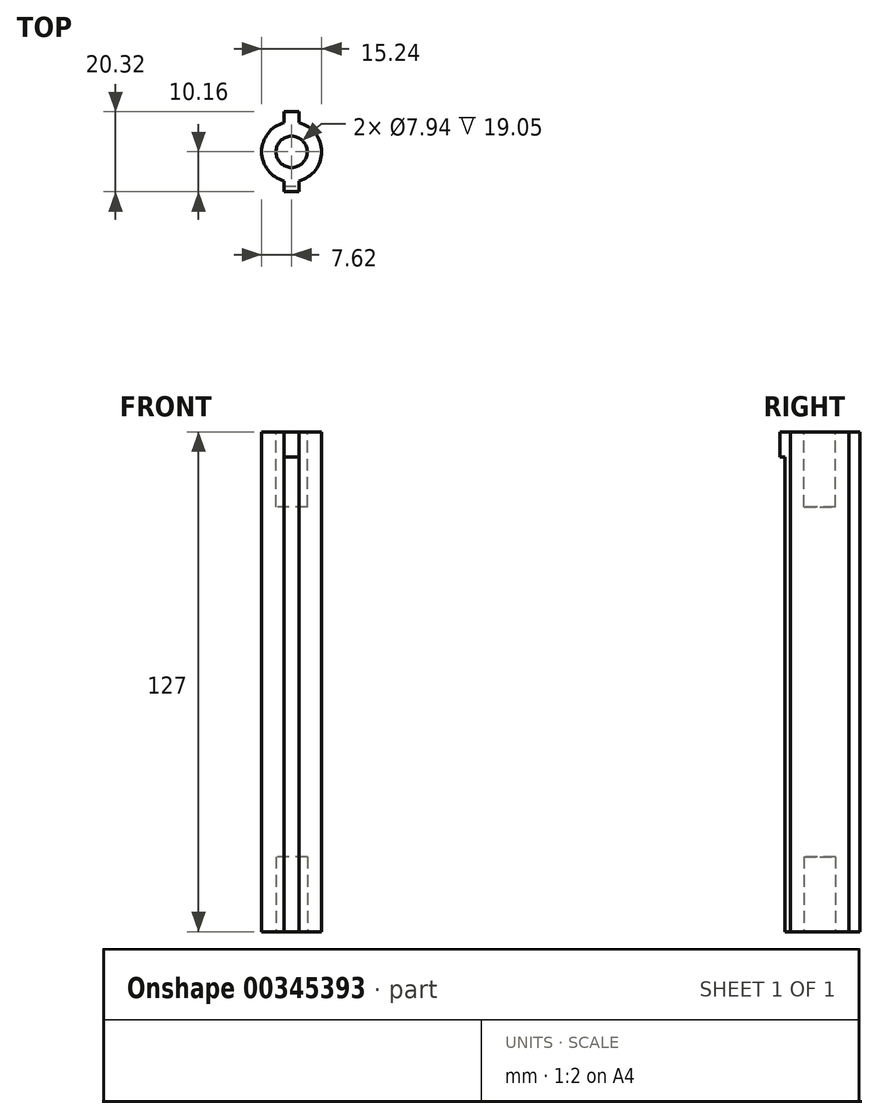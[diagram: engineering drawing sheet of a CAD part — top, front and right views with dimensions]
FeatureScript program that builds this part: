
annotation { "Feature Type Name" : "Feature", "Feature Type Description" : "" }
export const myFeature = defineFeature(function(context is Context, id is Id, definition is map)
    precondition{}
    {
        {
            var Q0;
            Q0=qCreatedBy(makeId("Top.planeOp"),FACE);
            var sketch = newSketch(context, id + "F0", { "sketchPlane" : qUnion([Q0])});
            skCircle(sketch, "E0", {"center": v(0, 0) * mm, "radius": 7.62 * mm});
            skSolve(sketch);
        }
        {
            var Q0;
            Q0=makeQuery(id+"F0.imprint","IMPRINT",FACE,{"disambiguationData":[TD([[makeQuery(id+"F0.imprint","IMPRINT",EDGE,{"derivedFrom":sQuery(id+"F0.wireOp",EDGE,"E0")}),1.0]])]});
            extrude(context, id + "F1", {"entities" : qUnion([Q0]), "depth" : 127 * mm});
        }
        {
            var Q0;
            Q0=makeQuery(id+"F1.opExtrude","CAP_FACE",FACE,{"disambiguationData":[OSD([sQuery(id+"F0.wireOp",EDGE,"E0")])],"isStart":false});
            var sketch = newSketch(context, id + "F2", { "sketchPlane" : qUnion([Q0])});
            skCircle(sketch, "E1", {"center": v(0, 0) * mm, "radius": 3.97 * mm});
            skSolve(sketch);
        }
        {
            var Q0;
            Q0=makeQuery(id+"F2.imprint","IMPRINT",FACE,{"disambiguationData":[TD([[makeQuery(id+"F2.imprint","IMPRINT",EDGE,{"derivedFrom":sQuery(id+"F2.wireOp",EDGE,"E1")}),1.0]])]});
            extrude(context, id + "F3", {"entities" : qUnion([Q0]), "operationType" : NewBodyOperationType.REMOVE, "oppositeDirection" : true, "depth" : 19.05 * mm});
        }
        {
            var Q0;
            Q0=qCreatedBy(makeId("Top.planeOp"),FACE);
            var sketch = newSketch(context, id + "F4", { "sketchPlane" : qUnion([Q0])});
            skLineSegment(sketch, "E2.bottom", {"start": v(-1.9, -10.16) * mm, "end": v(1.9, -10.16) * mm});
            skLineSegment(sketch, "E2.top", {"start": v(-1.9, 10.16) * mm, "end": v(1.9, 10.16) * mm});
            skLineSegment(sketch, "E2.left", {"start": v(-1.9, -10.16) * mm, "end": v(-1.9, 10.16) * mm});
            skLineSegment(sketch, "E2.right", {"start": v(1.9, -10.16) * mm, "end": v(1.9, 10.16) * mm});
            skPoint(sketch, "E2.middle", {"position": v(0, 0) * mm});
            skSolve(sketch);
        }
        {
            var Q0;
            Q0=makeQuery(id+"F4.imprint","IMPRINT",FACE,{"disambiguationData":[TD([[makeQuery(id+"F4.imprint","IMPRINT",EDGE,{"derivedFrom":sQuery(id+"F4.wireOp",EDGE,"E2.bottom")}),1.0]])]});
            extrude(context, id + "F5", {"entities" : qUnion([Q0]), "operationType" : NewBodyOperationType.ADD, "depth" : 127 * mm});
        }
        {
            var Q0;
            Q0=makeQuery(id+"F5.boolean.opBoolean","MERGE",FACE,{"derivedFrom":[makeQuery(id+"F1.opExtrude","CAP_FACE",FACE,{"disambiguationData":[OSD([sQuery(id+"F0.wireOp",EDGE,"E0")])],"isStart":false}),makeQuery(id+"F5.opExtrude","CAP_FACE",FACE,{"disambiguationData":[OSD([sQuery(id+"F4.wireOp",EDGE,"E2.bottom"),sQuery(id+"F4.wireOp",EDGE,"E2.top"),sQuery(id+"F4.wireOp",EDGE,"E2.left"),sQuery(id+"F4.wireOp",EDGE,"E2.right")])],"isStart":false})]});
            var sketch = newSketch(context, id + "F6", { "sketchPlane" : qUnion([Q0])});
            skCircle(sketch, "E3", {"center": v(0, 0) * mm, "radius": 3.97 * mm});
            skSolve(sketch);
        }
        {
            var Q0;
            {var subQ2=makeQuery(id+"F3.boolean.opBoolean","COPY",FACE,{"derivedFrom":makeQuery(id+"F3.opExtrude","SWEPT_FACE",FACE,{"disambiguationData":[OSD([sQuery(id+"F2.wireOp",EDGE,"E1")])]})});var subQ4=sQuery(id+"F4.wireOp",EDGE,"E2.left");var subQ6=makeQuery(id+"F5.boolean.opBoolean","SPLIT",EDGE,{"disambiguationData":[TD([subQ2])],"derivedFrom":makeQuery(id+"F5.opExtrude","CAP_EDGE",EDGE,{"disambiguationData":[OSD([subQ4])],"isStart":false})});Q0=makeQuery(id+"F6.imprint","IMPRINT",FACE,{"disambiguationData":[TD([[makeQuery(id+"F6.imprint","IMPRINT",EDGE,{"derivedFrom":subQ6}),-1.0]])]});}
            extrude(context, id + "F7", {"entities" : qUnion([Q0]), "operationType" : NewBodyOperationType.REMOVE, "oppositeDirection" : true, "depth" : 19.05 * mm});
        }
        {
            var Q0;
            Q0=qCreatedBy(makeId("Top.planeOp"),FACE);
            var sketch = newSketch(context, id + "F8", { "sketchPlane" : qUnion([Q0])});
            skCircle(sketch, "E4", {"center": v(0, 0) * mm, "radius": 3.97 * mm});
            skSolve(sketch);
        }
        {
            var Q0;
            Q0=makeQuery(id+"F8.imprint","IMPRINT",FACE,{"disambiguationData":[TD([[makeQuery(id+"F8.imprint","IMPRINT",EDGE,{"derivedFrom":sQuery(id+"F8.wireOp",EDGE,"E4")}),1.0]])]});
            extrude(context, id + "F9", {"entities" : qUnion([Q0]), "operationType" : NewBodyOperationType.REMOVE, "depth" : 19.05 * mm});
        }
        {
            var Q0;
            Q0=makeQuery(id+"F5.boolean.opBoolean","MERGE",FACE,{"derivedFrom":[makeQuery(id+"F1.opExtrude","CAP_FACE",FACE,{"disambiguationData":[OSD([sQuery(id+"F0.wireOp",EDGE,"E0")])],"isStart":true}),makeQuery(id+"F5.opExtrude","CAP_FACE",FACE,{"disambiguationData":[OSD([sQuery(id+"F4.wireOp",EDGE,"E2.bottom"),sQuery(id+"F4.wireOp",EDGE,"E2.top"),sQuery(id+"F4.wireOp",EDGE,"E2.left"),sQuery(id+"F4.wireOp",EDGE,"E2.right")])],"isStart":true})]});
            var sketch = newSketch(context, id + "F10", { "sketchPlane" : qUnion([Q0])});
            skLineSegment(sketch, "E5.bottom", {"start": v(-1.9, 10.16) * mm, "end": v(1.9, 10.16) * mm});
            skLineSegment(sketch, "E5.top", {"start": v(-1.9, 8.77) * mm, "end": v(1.9, 8.77) * mm});
            skLineSegment(sketch, "E5.left", {"start": v(-1.9, 10.16) * mm, "end": v(-1.9, 8.77) * mm});
            skLineSegment(sketch, "E5.right", {"start": v(1.9, 10.16) * mm, "end": v(1.9, 8.77) * mm});
            skSolve(sketch);
        }
        {
            var Q0;
            Q0 = qSketchRegion(id + "F10", true);
            extrude(context, id + "F11", {"entities" : qUnion([Q0]), "operationType" : NewBodyOperationType.REMOVE, "oppositeDirection" : true, "depth" : 120.65 * mm});
        }
    });
